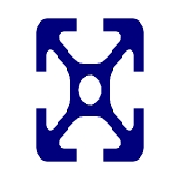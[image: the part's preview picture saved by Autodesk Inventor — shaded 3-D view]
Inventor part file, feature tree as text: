
AUTODESK INVENTOR PART (.ipt)
format: ipt  version: 2020 (Build 240168000, 168)  size: 277,504 bytes
history: native  units: mm
features: other x16, sketch x8, plane x1, split x1
ambient origin geometry x8: Origin, YZ Plane, XZ Plane, XY Plane, X Axis, Y Axis, Z Axis, Center Point
bodies: Body (feature_tree)
feature tree (26):
  other  "Řízená délka"
  other  "Těleso1"
  other  "Start Plane"
  other  "End Plane"
  other  "iFeatureSketch"
  other  "DRAZKA_20:1"
  other  "DRAZKA_20:2"
  other  "DRAZKA_20:3"
  other  "DRAZKA_20:4"
  other  "DIRA_20:1"
  other  "DRAZKA_20:1Axis"
  other  "DRAZKA_20:2Axis"
  other  "DRAZKA_20:3Axis"
  other  "DRAZKA_20:4Axis"
  other  "DIRA_20:1Axis"
  plane  "Work Plane5"
  split  "Split1"
  sketch  "Sketch"  dims[d2=20.0mm d3=20.0mm d4=2.0mm d9=10.0mm d10=300.0mm d11=0.13mm d12=0.0mm d15=0.83mm d16=0.83mm d17=9.8mm d18=3.0mm d19=4.55mm d20=45.0deg d21=5.2mm d22=1.8mm d24=1.0mm d26=0.83mm d27=0.83mm d28=9.8mm d29=3.0mm d30=4.55mm d31=45.0deg d32=5.2mm d33=1.8mm d35=1.0mm d37=0.83mm d38=0.83mm d39=9.8mm d40=3.0mm d41=4.55mm d42=45.0deg d43=5.2mm d44=1.8mm d46=1.0mm d48=0.83mm d49=0.83mm d50=9.8mm d51=3.0mm d52=4.55mm d53=45.0deg d54=5.2mm d55=1.8mm d57=1.0mm d59=4.3mm d60=0.0mm d61=0.0mm d62=0.0mm d63=0.0mm d64=0.0mm d65=0.0mm d66=0.0mm d67=0.0mm d76=90.0deg d14=290.0mm]
  sketch  "Náčrt11"
  other  "Pracovní rovina4"
  sketch  "Náčrt12"
  sketch  "Náčrt6"
  sketch  "Náčrt7"
  sketch  "Náčrt8"
  sketch  "Náčrt9"
  sketch  "Náčrt10"
